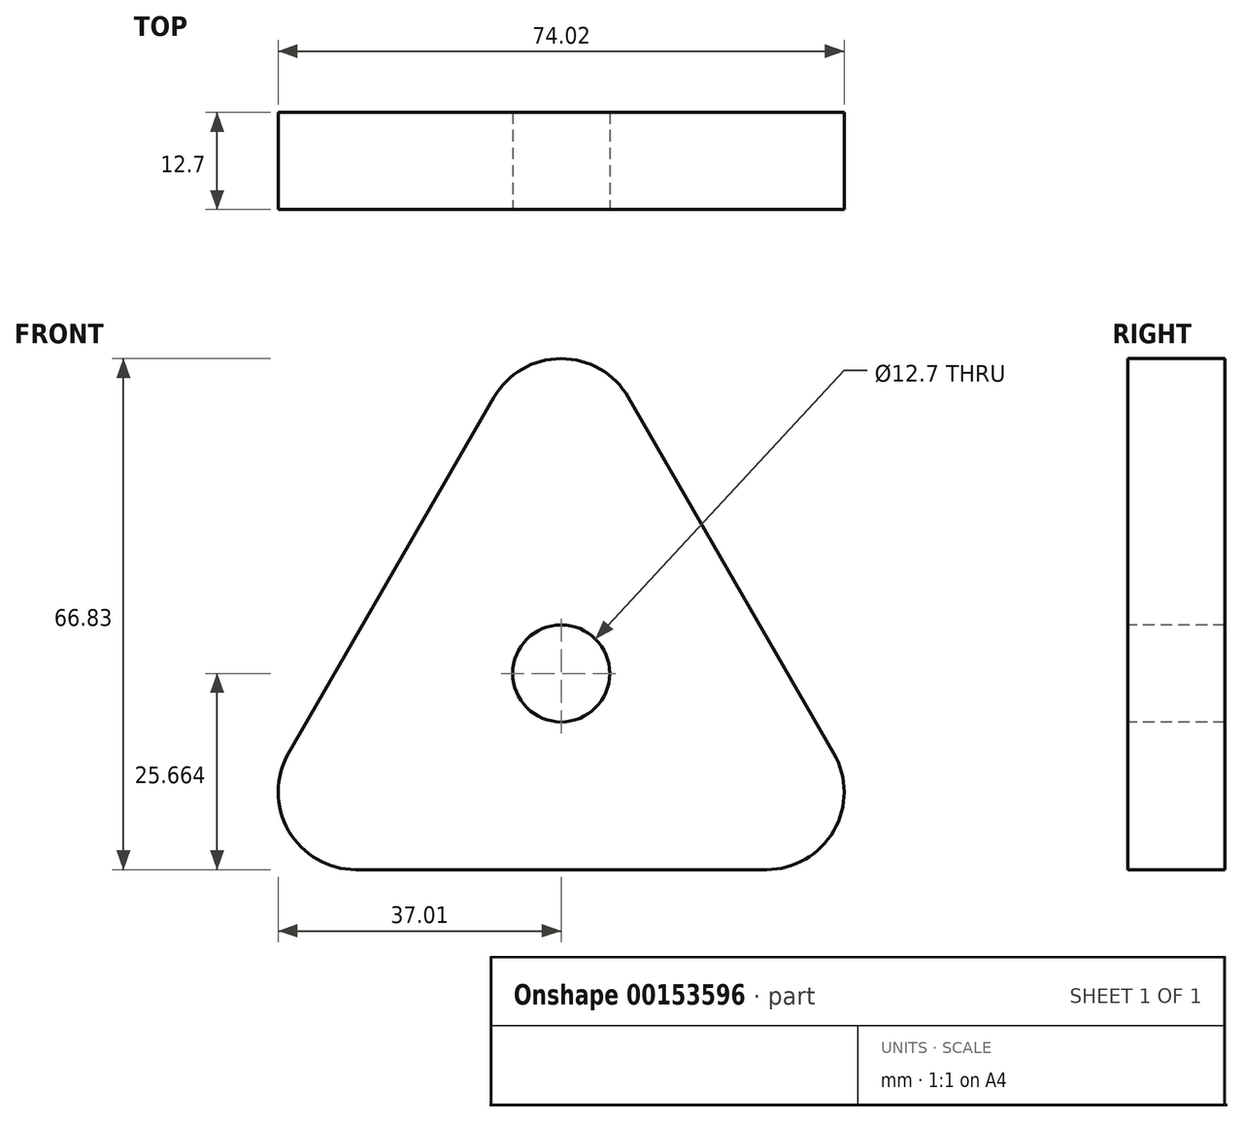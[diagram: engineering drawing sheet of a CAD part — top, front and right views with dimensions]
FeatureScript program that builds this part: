
annotation { "Feature Type Name" : "Feature", "Feature Type Description" : "" }
export const myFeature = defineFeature(function(context is Context, id is Id, definition is map)
    precondition{}
    {
        {
            var Q0;
            Q0=qCreatedBy(makeId("Front.planeOp"),FACE);
            var sketch = newSketch(context, id + "F0", { "sketchPlane" : qUnion([Q0])});
            skLineSegment(sketch, "E0", {"start": v(0, 0) * mm, "end": v(0, 25.4) * mm, "construction": true});
            skLineSegment(sketch, "E1", {"start": v(0, 0) * mm, "end": v(0, -25.4) * mm, "construction": true});
            skLineSegment(sketch, "E2", {"start": v(-8.8, 10.16) * mm, "end": v(-35.65, -36.35) * mm});
            skLineSegment(sketch, "E3", {"start": v(8.8, 10.16) * mm, "end": v(35.65, -36.35) * mm});
            skLineSegment(sketch, "E4", {"start": v(-26.85, -51.59) * mm, "end": v(26.85, -51.59) * mm});
            skLineSegment(sketch, "E5", {"start": v(-33.48, 0) * mm, "end": v(43.4, 0) * mm, "construction": true});
            skPoint(sketch, "E6.visualSharp", {"position": v(0, 25.4) * mm});
            skArc(sketch, "E6.filletArc", {"start": v(8.8, 10.16) * mm, "mid": v(0, 15.24) * mm, "end": v(-8.8, 10.16) * mm});
            skPoint(sketch, "E7.visualSharp", {"position": v(-44.45, -51.59) * mm});
            skArc(sketch, "E7.filletArc", {"start": v(-35.65, -36.35) * mm, "mid": v(-35.65, -46.5) * mm, "end": v(-26.85, -51.59) * mm});
            skPoint(sketch, "E8.visualSharp", {"position": v(44.45, -51.59) * mm});
            skArc(sketch, "E8.filletArc", {"start": v(26.85, -51.59) * mm, "mid": v(35.65, -46.5) * mm, "end": v(35.65, -36.35) * mm});
            skLineSegment(sketch, "E9", {"start": v(0, 0) * mm, "end": v(14.66, 0) * mm, "construction": true});
            skLineSegment(sketch, "E10", {"start": v(0, 0) * mm, "end": v(-14.66, 0) * mm, "construction": true});
            skSolve(sketch);
        }
        {
            var Q0;
            Q0=qSketchRegion(id+"F0",true);
            extrude(context, id + "F1", {"entities" : qUnion([Q0]), "depth" : 12.7 * mm});
        }
        {
            var Q0;
            Q0=makeQuery(id+"F1.opExtrude","CAP_FACE",FACE,{"disambiguationData":[OSD([sQuery(id+"F0.wireOp",EDGE,"E2"),sQuery(id+"F0.wireOp",EDGE,"E3"),sQuery(id+"F0.wireOp",EDGE,"E4"),sQuery(id+"F0.wireOp",EDGE,"E6.filletArc"),sQuery(id+"F0.wireOp",EDGE,"E7.filletArc"),sQuery(id+"F0.wireOp",EDGE,"E8.filletArc")])],"isStart":false});
            var sketch = newSketch(context, id + "F2", { "sketchPlane" : qUnion([Q0])});
            skLineSegment(sketch, "E11", {"start": v(-35.65, -46.5) * mm, "end": v(0, -25.93) * mm, "construction": true});
            skLineSegment(sketch, "E12", {"start": v(0, 15.24) * mm, "end": v(0, -25.93) * mm, "construction": true});
            skLineSegment(sketch, "E13", {"start": v(35.65, -46.5) * mm, "end": v(0, -25.93) * mm, "construction": true});
            skCircle(sketch, "E14", {"center": v(0, -25.93) * mm, "radius": 6.35 * mm});
            skSolve(sketch);
        }
        {
            var Q0;
            Q0=makeQuery(id+"F2.imprint","IMPRINT",FACE,{"disambiguationData":[TD([[makeQuery(id+"F2.imprint","IMPRINT",EDGE,{"derivedFrom":sQuery(id+"F2.wireOp",EDGE,"E14")}),1.0]])]});
            var Q1;
            Q1=sQuery(id+"F2.wireOp",EDGE,"QFnR3G9j-Mm4j-uMxI-Hg1k-K7k4eNcVNfiD");
            extrude(context, id + "F3", {"entities" : qUnion([Q0]), "operationType" : NewBodyOperationType.REMOVE, "surfaceEntities" : qUnion([Q1]), "oppositeDirection" : true, "depth" : 25.4 * mm});
        }
    });
